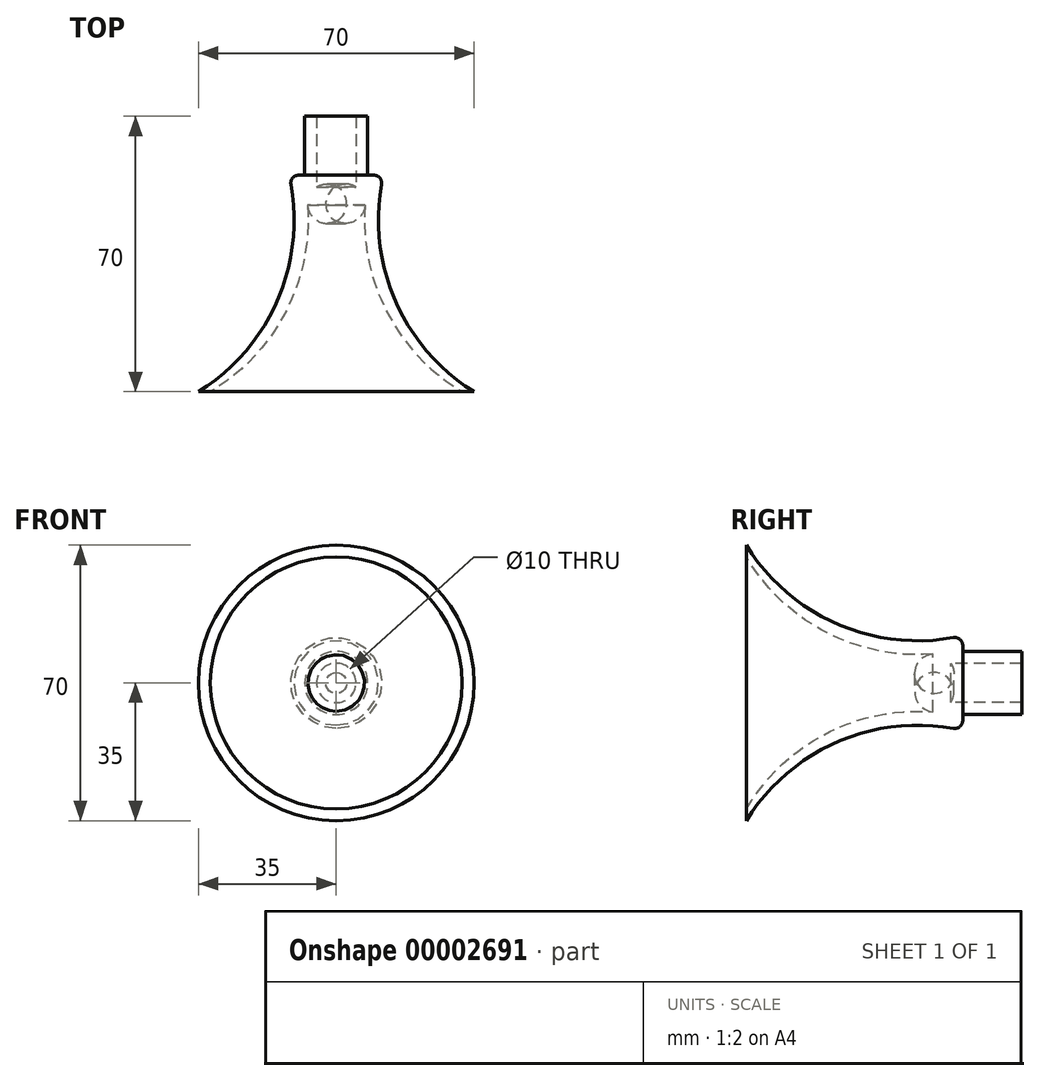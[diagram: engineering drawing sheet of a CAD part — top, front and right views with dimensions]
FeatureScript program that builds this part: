
annotation { "Feature Type Name" : "Feature", "Feature Type Description" : "" }
export const myFeature = defineFeature(function(context is Context, id is Id, definition is map)
    precondition{}
    {
        {
            var Q0;
            Q0=qCreatedBy(makeId("Top.planeOp"),FACE);
            var sketch = newSketch(context, id + "F0", { "sketchPlane" : qUnion([Q0])});
            skLineSegment(sketch, "E0", {"start": v(0, -35) * mm, "end": v(0, 35) * mm, "construction": true});
            skLineSegment(sketch, "E1", {"start": v(-8, 35) * mm, "end": v(-8, 20) * mm});
            skLineSegment(sketch, "E2", {"start": v(-8, 20) * mm, "end": v(-12, 20) * mm});
            skPoint(sketch, "E3", {"position": v(-35, -35) * mm});
            skArc(sketch, "E4", {"start": v(-35, -35) * mm, "mid": v(-14.69, -11.19) * mm, "end": v(-12, 20) * mm});
            skLineSegment(sketch, "E5", {"start": v(-8, 35) * mm, "end": v(-5, 35) * mm});
            skLineSegment(sketch, "E6", {"start": v(-5, 35) * mm, "end": v(-5, 17) * mm});
            skLineSegment(sketch, "E7", {"start": v(-5, 17) * mm, "end": v(-7.88, 17) * mm});
            skLineSegment(sketch, "E8", {"start": v(-35, -35) * mm, "end": v(-32, -35) * mm});
            skArc(sketch, "E9", {"start": v(-32, -35) * mm, "mid": v(-11.88, -12.74) * mm, "end": v(-7.88, 17) * mm});
            skSolve(sketch);
        }
        {
            var Q0;
            Q0=makeQuery(id+"F0.imprint","IMPRINT",FACE,{"disambiguationData":[TD([[makeQuery(id+"F0.imprint","IMPRINT",EDGE,{"derivedFrom":sQuery(id+"F0.wireOp",EDGE,"E1")}),1.0]])]});
            var Q1;
            Q1=sQuery(id+"F0.wireOp",EDGE,"E0");
            revolve(context, id + "F1", {"entities" : qUnion([Q0]), "axis" : qUnion([Q1]), "revolveType" : RevolveType.FULL});
        }
        {
            var Q0;
            Q0=makeQuery(id+"F1.opRevolve","SWEPT_EDGE",EDGE,{"disambiguationData":[OSD([sQuery(id+"F0.wireOp",EDGE,"E2"),sQuery(id+"F0.wireOp",EDGE,"E4")])]});
            fillet(context, id + "F2", {"entities" : qUnion([Q0]), "radius" : 2 * mm, "tangentPropagation" : true, "allowEdgeOverflow" : false});
        }
        {
            var Q0;
            Q0=makeQuery(id+"F1.opRevolve","SWEPT_EDGE",EDGE,{"disambiguationData":[OSD([sQuery(id+"F0.wireOp",EDGE,"E7"),sQuery(id+"F0.wireOp",EDGE,"E9")])]});
            fillet(context, id + "F3", {"entities" : qUnion([Q0]), "radius" : 5 * mm, "tangentPropagation" : true, "allowEdgeOverflow" : false});
        }
    });
